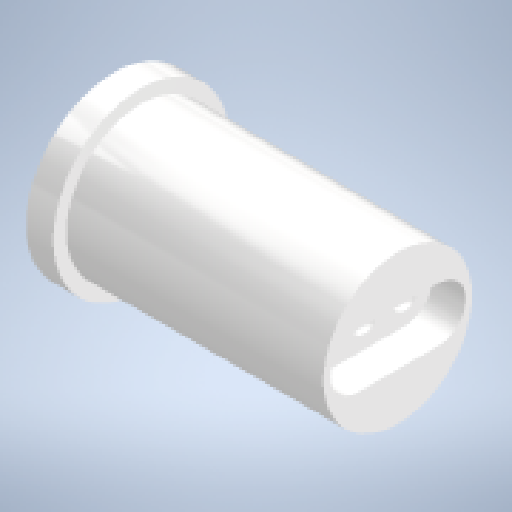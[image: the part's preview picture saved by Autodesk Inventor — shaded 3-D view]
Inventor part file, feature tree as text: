
AUTODESK INVENTOR PART (.ipt)
format: ipt  version: 2023 (Build 270158000, 158)  size: 189,440 bytes
history: native  units: mm
features: sketch x3, revolve x2, pattern_linear x2, extrude x1
ambient origin geometry x8: Origin, YZ Plane, XZ Plane, XY Plane, X Axis, Y Axis, Z Axis, Center Point
bodies: Solid1 (feature_tree)
feature tree (8):
  revolve  "Revolution1"  [1 undecoded]
  revolve  "Revolution2"  [1 undecoded]
  pattern_linear  "Rectangular Pattern1"  Spacing1=5.5mm  [1 undecoded]
  pattern_linear  "Rectangular Pattern2"  Spacing1=8.0mm  [1 undecoded]
  extrude  "Extrusion1"  Depth=4.0mm
  sketch  "Sketch1"  dims[d0=22.0mm d1=38.0mm]
  sketch  "Sketch3"  dims[d2=26.0mm d3=4.0mm]
  sketch  "Sketch4"  dims[d4=90.0deg d16=5.5mm d17=8.0mm d18=4.0mm d19=5.0mm d20=5.0mm d21=90.0deg d22=20.0mm d24=6.0mm d25=20.0mm d27=6.0mm d28=10.0mm d29=0.0mm]
note: 4 required parameter values undecoded (feature->parameter linkage not recoverable at this tier; creation-order binding heuristic only, values carry confidence <= 0.55)